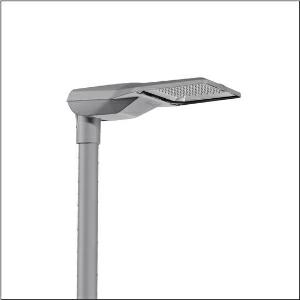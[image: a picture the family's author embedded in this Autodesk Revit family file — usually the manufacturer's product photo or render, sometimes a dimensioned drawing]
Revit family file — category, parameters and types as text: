
# Revit family: streetlight_sl_21_iq_midi___st0_5a_5xe3b41g08nb_d4f3
name_source: partatom
category: Lighting Fixtures
units: mm (PartAtom-declared; Revit-internal decimal feet)

## family parameters
Cut with Voids When Loaded = No
Host = Face
Light Source = No
Part Type = Normal
Room Calculation Point = No
Round Connector Dimension = Use Diameter
Shared = No

## types (1)
- --- (1 x LED, 24250 lm, 155.5 W, 4000K)
    Apparent Load = 155 VA
    CIE Flux Codes = 43 76 97 100 100
    Color Rendering = 70
    Color Temperature = 4000K
    Default Elevation = 1800 mm
    Description = Streetlight SL 21 iQ midi, mast luminaire, primary light control with lens, of PMMA, primary optical cover: cover, of toughened safety glass, transparent, light distribution: ST0.5a, light emission: direct distribution, primary light characteristic: asymmetric, installation type: post-top, side-entry, LED, High Power LED, rated luminous flux: 24.250lm, luminous efficacy: 156lm/W, light colour: 740, colour temperature: 4000K, control: Street-Remote, Auto-Match, Temp-Guard, Lumen-Switch, Night-Set, Smart-Wire, Light-Fading, Desk-Remote (wireless, voltage-free reading and setting of iQ features in the workshop via application-optimized NFC function/RFID function), optimised constant luminous flux control (CLO 2.0), presetting dimming linear, mains connection: 230..240V, AC, 50/60Hz, start of lifetime: 156W, end of service life: 162W, reduction: 69W, luminaire housing, of diecast aluminium, powder-coated, Siteco® metallic grey (DB 702S), corrosivity category C5 mid according to DIN EN ISO 12944, please order mast flange separately, inclination adjustable: 0°, 5°, 10°, 15°, sealing non-destructively replaceable, multi-level sealing system, length: 644mm, width: 335mm, height: 110mm, mast flange for spigot size: 42mm (side-entry): 5XC10008XM4, 60/48mm (side-entry/post-top): 5XC10108XM2, 76/60mm (side-entry/post-top): 5XC10108XM1, protection rating (complete): IP66, insulation class (complete): insulation class II (safety insulation), certification: CE, ENEC, ENEC+, VDE, impact resistance: IK09, permissible operating ambient temperature for outdoor applications: -40..+50°C, standard-compliant lighting for roads and squares, packaging unit: 1 piece

Light Distribution: ST0.5a
    Height = 111 mm
    Lamp = 1 x LED
    Lamp Light Flux = 24250 lm
    Lamp Power = 155.5 W
    Lamp count = 1
    Length = 644 mm
    Luminous efficacy = 156 lm/W
    Manufacturer = Siteco
    ModVariant = No
    Model = 5XE3B41G08NB
    Number of Poles = 1
    OnlyDefault = Yes
    Power Factor = 1
    Product Name = Streetlight SL 21 iQ midi | ST0.5a
    Product group = mast luminaire | pylon top
    ProductGroupID = 6100
    Protection Class = Protection class II
    Protection Degree = IP 66
    RLX_Detail_Level = 1
    RLX_Emergency_Light_Flux = 0 lm
    RLX_Emergency_Type = 0
    RLX_Emergency_Type_DB = No
    RlxData = <blob elided: 102265 chars, md5=9a2bae37>
    Socket = socket
    Standby Power = 0 W
    System Light Flux = 24250 lm
    System Power = 155 W
    Type Comments = factory setting: luminous flux: 100 % | dim-lin: 254 | 823 mA
    Type Image = l_1004298.jpg
    URL = http://relux.com
    VarID = @adj_104389
    Voltage = 0 V
    Weight = 0.00 kg
    Width = 336 mm

## geometry (parser evidence)
native form markers: Blend x4, Sweep x10
no freeform markers — native parametric forms only
